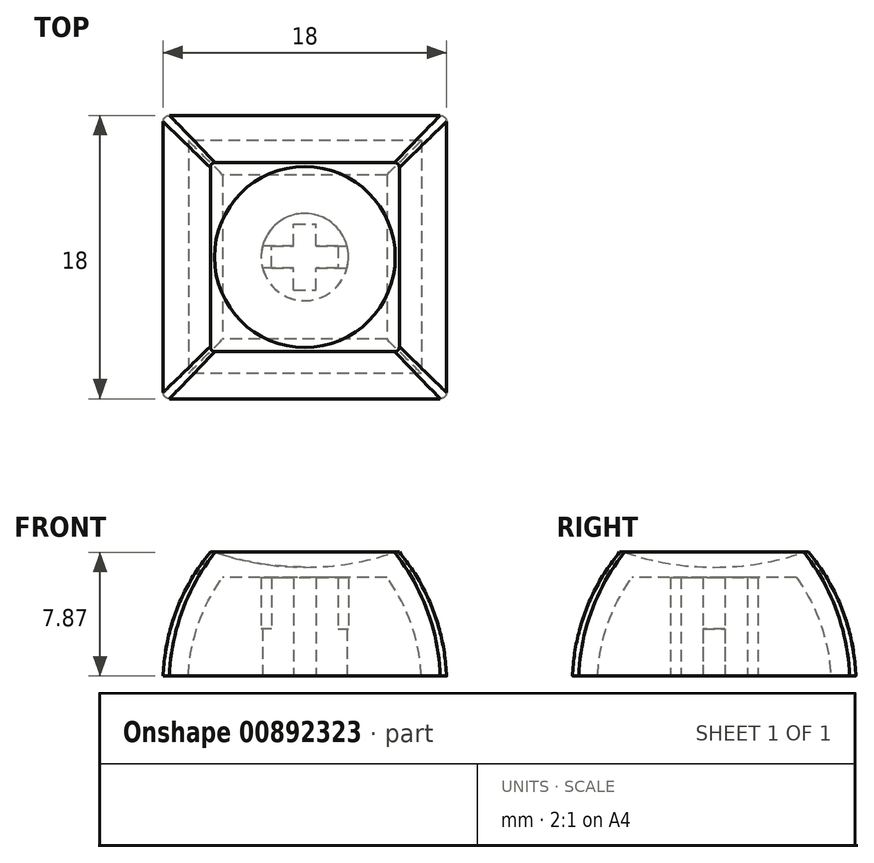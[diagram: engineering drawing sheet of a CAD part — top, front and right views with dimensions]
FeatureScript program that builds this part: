
annotation { "Feature Type Name" : "Feature", "Feature Type Description" : "" }
export const myFeature = defineFeature(function(context is Context, id is Id, definition is map)
    precondition{}
    {
        {
            var Q0;
            Q0=qCreatedBy(makeId("Top.planeOp"),FACE);
            var sketch = newSketch(context, id + "F0", { "sketchPlane" : qUnion([Q0])});
            skLineSegment(sketch, "E0.bottom", {"start": v(9, 9) * mm, "end": v(-9, 9) * mm});
            skLineSegment(sketch, "E0.top", {"start": v(9, -9) * mm, "end": v(-9, -9) * mm});
            skLineSegment(sketch, "E0.left", {"start": v(9, 9) * mm, "end": v(9, -9) * mm});
            skLineSegment(sketch, "E0.right", {"start": v(-9, 9) * mm, "end": v(-9, -9) * mm});
            skPoint(sketch, "E0.middle", {"position": v(0, 0) * mm});
            skSolve(sketch);
        }
        {
            var Q0;
            Q0=makeQuery(id+"F0.imprint","IMPRINT",FACE,{"disambiguationData":[TD([[makeQuery(id+"F0.imprint","IMPRINT",EDGE,{"derivedFrom":sQuery(id+"F0.wireOp",EDGE,"E0.bottom")}),1.0]])]});
            extrude(context, id + "F1", {"entities" : qUnion([Q0]), "depth" : 7.87 * mm, "offsetDistance" : 25 * mm});
        }
        {
            var Q0;
            Q0=makeQuery(id+"F1.opExtrude","SWEPT_FACE",FACE,{"disambiguationData":[OSD([sQuery(id+"F0.wireOp",EDGE,"E0.top")])]});
            var sketch = newSketch(context, id + "F2", { "sketchPlane" : qUnion([Q0])});
            skLineSegment(sketch, "E1", {"start": v(-9, 7.87) * mm, "end": v(-7.23, 6.1) * mm});
            skLineSegment(sketch, "E2", {"start": v(9, 7.87) * mm, "end": v(7.23, 6.1) * mm});
            skLineSegment(sketch, "E3", {"start": v(-9, 7.87) * mm, "end": v(-6, 7.87) * mm});
            skLineSegment(sketch, "E4", {"start": v(9, 7.87) * mm, "end": v(6, 7.87) * mm});
            skArc(sketch, "E5", {"start": v(-6, 7.87) * mm, "mid": v(-8.15, 4.18) * mm, "end": v(-9, 0) * mm});
            skArc(sketch, "E6", {"start": v(9, 0) * mm, "mid": v(8.15, 4.18) * mm, "end": v(6, 7.87) * mm});
            skLineSegment(sketch, "E7", {"start": v(-6, 7.87) * mm, "end": v(6, 7.87) * mm});
            skLineSegment(sketch, "E8", {"start": v(0, 7.87) * mm, "end": v(0, 7.17) * mm});
            skLineSegment(sketch, "E9", {"start": v(-6, 7.87) * mm, "end": v(-6, 7.87) * mm});
            skLineSegment(sketch, "E10", {"start": v(6, 7.87) * mm, "end": v(6, 7.87) * mm});
            skArc(sketch, "E11", {"start": v(-6, 7.87) * mm, "mid": v(0, 7.17) * mm, "end": v(6, 7.87) * mm});
            skSolve(sketch);
        }
        {
            var Q0;
            Q0=makeQuery(id+"F1.opExtrude","SWEPT_FACE",FACE,{"disambiguationData":[OSD([sQuery(id+"F0.wireOp",EDGE,"E0.right")])]});
            var sketch = newSketch(context, id + "F3", { "sketchPlane" : qUnion([Q0])});
            skLineSegment(sketch, "E12", {"start": v(-9, 7.87) * mm, "end": v(-7.23, 6.1) * mm});
            skLineSegment(sketch, "E13", {"start": v(9, 7.87) * mm, "end": v(7.23, 6.1) * mm});
            skLineSegment(sketch, "E14", {"start": v(-9, 7.87) * mm, "end": v(-6, 7.87) * mm});
            skLineSegment(sketch, "E15", {"start": v(9, 7.87) * mm, "end": v(6, 7.87) * mm});
            skArc(sketch, "E16", {"start": v(-6, 7.87) * mm, "mid": v(-8.15, 4.18) * mm, "end": v(-9, 0) * mm});
            skArc(sketch, "E17", {"start": v(9, 0) * mm, "mid": v(8.15, 4.18) * mm, "end": v(6, 7.87) * mm});
            skLineSegment(sketch, "E18", {"start": v(-6, 7.87) * mm, "end": v(-6, 7.87) * mm});
            skLineSegment(sketch, "E19", {"start": v(6, 7.87) * mm, "end": v(6, 7.87) * mm});
            skLineSegment(sketch, "E20", {"start": v(0, 7.87) * mm, "end": v(0, 7.17) * mm});
            skArc(sketch, "E21", {"start": v(-6, 7.87) * mm, "mid": v(0, 7.17) * mm, "end": v(6, 7.87) * mm});
            skSolve(sketch);
        }
        {
            var Q0;
            {var subQ0=sQuery(id+"F3.wireOp",EDGE,"E12");Q0=makeQuery(id+"F3.imprint","IMPRINT",FACE,{"disambiguationData":[TD([[makeQuery(id+"F3.imprint","IMPRINT",EDGE,{"derivedFrom":subQ0}),1.0]])]});}
            var Q1;
            {var subQ0=sQuery(id+"F3.wireOp",EDGE,"E12");Q1=makeQuery(id+"F3.imprint","IMPRINT",FACE,{"disambiguationData":[TD([[makeQuery(id+"F3.imprint","IMPRINT",EDGE,{"derivedFrom":subQ0}),-1.0]])]});}
            var Q2;
            {var subQ0=sQuery(id+"F3.wireOp",EDGE,"E13");Q2=makeQuery(id+"F3.imprint","IMPRINT",FACE,{"disambiguationData":[TD([[makeQuery(id+"F3.imprint","IMPRINT",EDGE,{"derivedFrom":subQ0}),-1.0]])]});}
            var Q3;
            {var subQ0=sQuery(id+"F3.wireOp",EDGE,"E13");Q3=makeQuery(id+"F3.imprint","IMPRINT",FACE,{"disambiguationData":[TD([[makeQuery(id+"F3.imprint","IMPRINT",EDGE,{"derivedFrom":subQ0}),1.0]])]});}
            extrude(context, id + "F4", {"entities" : qUnion([Q0, Q1, Q2, Q3]), "operationType" : NewBodyOperationType.REMOVE, "oppositeDirection" : true, "depth" : 25 * mm, "offsetDistance" : 25 * mm});
        }
        {
            var Q0;
            {var subQ0=sQuery(id+"F2.wireOp",EDGE,"E1");Q0=makeQuery(id+"F2.imprint","IMPRINT",FACE,{"disambiguationData":[TD([[makeQuery(id+"F2.imprint","IMPRINT",EDGE,{"derivedFrom":subQ0}),-1.0]])]});}
            var Q1;
            {var subQ0=sQuery(id+"F2.wireOp",EDGE,"E1");Q1=makeQuery(id+"F2.imprint","IMPRINT",FACE,{"disambiguationData":[TD([[makeQuery(id+"F2.imprint","IMPRINT",EDGE,{"derivedFrom":subQ0}),1.0]])]});}
            var Q2;
            {var subQ0=sQuery(id+"F2.wireOp",EDGE,"E2");Q2=makeQuery(id+"F2.imprint","IMPRINT",FACE,{"disambiguationData":[TD([[makeQuery(id+"F2.imprint","IMPRINT",EDGE,{"derivedFrom":subQ0}),-1.0]])]});}
            var Q3;
            {var subQ0=sQuery(id+"F2.wireOp",EDGE,"E2");Q3=makeQuery(id+"F2.imprint","IMPRINT",FACE,{"disambiguationData":[TD([[makeQuery(id+"F2.imprint","IMPRINT",EDGE,{"derivedFrom":subQ0}),1.0]])]});}
            extrude(context, id + "F5", {"entities" : qUnion([Q0, Q1, Q2, Q3]), "operationType" : NewBodyOperationType.REMOVE, "oppositeDirection" : true, "depth" : 25 * mm, "offsetDistance" : 25 * mm});
        }
        {
            var Q0;
            Q0=makeQuery(id+"F1.opExtrude","CAP_FACE",FACE,{"disambiguationData":[OSD([sQuery(id+"F0.wireOp",EDGE,"E0.bottom"),sQuery(id+"F0.wireOp",EDGE,"E0.top"),sQuery(id+"F0.wireOp",EDGE,"E0.left"),sQuery(id+"F0.wireOp",EDGE,"E0.right")])],"isStart":true});
            shell(context, id + "F6", {"entities" : qUnion([Q0]), "thickness" : 1.6 * mm});
        }
        {
            var Q0;
            Q0=makeQuery(id+"F1.opExtrude","CAP_FACE",FACE,{"disambiguationData":[OSD([sQuery(id+"F0.wireOp",EDGE,"E0.bottom"),sQuery(id+"F0.wireOp",EDGE,"E0.top"),sQuery(id+"F0.wireOp",EDGE,"E0.left"),sQuery(id+"F0.wireOp",EDGE,"E0.right")])],"isStart":true});
            var sketch = newSketch(context, id + "F7", { "sketchPlane" : qUnion([Q0])});
            skLineSegment(sketch, "E22.bottom", {"start": v(0, 0) * mm, "end": v(0.7, 0) * mm});
            skLineSegment(sketch, "E22.top", {"start": v(0, 2.1) * mm, "end": v(0.7, 2.1) * mm});
            skLineSegment(sketch, "E22.left", {"start": v(0, 0) * mm, "end": v(0, 2.1) * mm});
            skLineSegment(sketch, "E22.right", {"start": v(0.7, 0) * mm, "end": v(0.7, 2.1) * mm});
            skLineSegment(sketch, "E23.bottom", {"start": v(0, 0) * mm, "end": v(-0.7, 0) * mm});
            skLineSegment(sketch, "E23.top", {"start": v(0, 2.1) * mm, "end": v(-0.7, 2.1) * mm});
            skLineSegment(sketch, "E23.right", {"start": v(-0.7, 0) * mm, "end": v(-0.7, 2.1) * mm});
            skLineSegment(sketch, "E24.bottom", {"start": v(0, 0) * mm, "end": v(2.1, 0) * mm});
            skLineSegment(sketch, "E24.top", {"start": v(0, 0.7) * mm, "end": v(2.1, 0.7) * mm});
            skLineSegment(sketch, "E24.left", {"start": v(0, 0) * mm, "end": v(0, 0.7) * mm});
            skLineSegment(sketch, "E24.right", {"start": v(2.1, 0) * mm, "end": v(2.1, 0.7) * mm});
            skLineSegment(sketch, "E25.top", {"start": v(0, -0.7) * mm, "end": v(2.1, -0.7) * mm});
            skLineSegment(sketch, "E25.left", {"start": v(0, 0) * mm, "end": v(0, -0.7) * mm});
            skLineSegment(sketch, "E25.right", {"start": v(2.1, 0) * mm, "end": v(2.1, -0.7) * mm});
            skLineSegment(sketch, "E26.bottom", {"start": v(0, 0) * mm, "end": v(-2.1, 0) * mm});
            skLineSegment(sketch, "E26.top", {"start": v(0, 0.7) * mm, "end": v(-2.1, 0.7) * mm});
            skLineSegment(sketch, "E26.right", {"start": v(-2.1, 0) * mm, "end": v(-2.1, 0.7) * mm});
            skLineSegment(sketch, "E27.top", {"start": v(0, -0.7) * mm, "end": v(-2.1, -0.7) * mm});
            skLineSegment(sketch, "E27.right", {"start": v(-2.1, 0) * mm, "end": v(-2.1, -0.7) * mm});
            skLineSegment(sketch, "E28.bottom", {"start": v(-0.7, 0) * mm, "end": v(0, 0) * mm});
            skLineSegment(sketch, "E28.top", {"start": v(-0.7, -2.1) * mm, "end": v(0, -2.1) * mm});
            skLineSegment(sketch, "E28.left", {"start": v(-0.7, 0) * mm, "end": v(-0.7, -2.1) * mm});
            skLineSegment(sketch, "E28.right", {"start": v(0, 0) * mm, "end": v(0, -2.1) * mm});
            skLineSegment(sketch, "E29.bottom", {"start": v(0.7, 0) * mm, "end": v(0, 0) * mm});
            skLineSegment(sketch, "E29.top", {"start": v(0.7, -2.1) * mm, "end": v(0, -2.1) * mm});
            skLineSegment(sketch, "E29.left", {"start": v(0.7, 0) * mm, "end": v(0.7, -2.1) * mm});
            skCircle(sketch, "E30", {"center": v(0, 0) * mm, "radius": 2.77 * mm});
            skSolve(sketch);
        }
        {
            var Q0;
            {var subQ12=sQuery(id+"F7.wireOp",EDGE,"E22.top");Q0=makeQuery(id+"F7.imprint","IMPRINT",FACE,{"disambiguationData":[TD([[makeQuery(id+"F7.imprint","IMPRINT",EDGE,{"derivedFrom":subQ12}),1.0]])]});}
            extrude(context, id + "F8", {"entities" : qUnion([Q0]), "operationType" : NewBodyOperationType.ADD, "oppositeDirection" : true, "depth" : 7 * mm, "offsetDistance" : 25 * mm});
        }
        {
            var Q0;
            Q0=makeQuery(id+"F8.opExtrude","CAP_FACE",FACE,{"disambiguationData":[OSD([sQuery(id+"F7.wireOp",EDGE,"E22.top"),sQuery(id+"F7.wireOp",EDGE,"E22.right"),sQuery(id+"F7.wireOp",EDGE,"E23.top"),sQuery(id+"F7.wireOp",EDGE,"E23.right"),sQuery(id+"F7.wireOp",EDGE,"E24.top"),sQuery(id+"F7.wireOp",EDGE,"E24.right"),sQuery(id+"F7.wireOp",EDGE,"E25.top"),sQuery(id+"F7.wireOp",EDGE,"E25.right"),sQuery(id+"F7.wireOp",EDGE,"E26.top"),sQuery(id+"F7.wireOp",EDGE,"E26.right"),sQuery(id+"F7.wireOp",EDGE,"E27.top"),sQuery(id+"F7.wireOp",EDGE,"E27.right"),sQuery(id+"F7.wireOp",EDGE,"E28.top"),sQuery(id+"F7.wireOp",EDGE,"E28.left"),sQuery(id+"F7.wireOp",EDGE,"E29.top"),sQuery(id+"F7.wireOp",EDGE,"E29.left"),sQuery(id+"F7.wireOp",EDGE,"E30")])],"isStart":true});
            var sketch = newSketch(context, id + "F9", { "sketchPlane" : qUnion([Q0])});
            skLineSegment(sketch, "E31", {"start": v(-2.1, 0.7) * mm, "end": v(-2.68, 0.7) * mm});
            skLineSegment(sketch, "E32", {"start": v(-2.1, -0.7) * mm, "end": v(-2.68, -0.7) * mm});
            skLineSegment(sketch, "E33", {"start": v(2.1, -0.7) * mm, "end": v(2.68, -0.7) * mm});
            skLineSegment(sketch, "E34", {"start": v(2.1, 0.7) * mm, "end": v(2.68, 0.7) * mm});
            skCircle(sketch, "E35", {"center": v(0, 0) * mm, "radius": 2.77 * mm});
            skSolve(sketch);
        }
        {
            var Q0;
            {var subQ0=sQuery(id+"F9.wireOp",EDGE,"E31");Q0=makeQuery(id+"F9.imprint","IMPRINT",FACE,{"disambiguationData":[TD([[makeQuery(id+"F9.imprint","IMPRINT",EDGE,{"derivedFrom":subQ0}),1.0]])]});}
            var Q1;
            {var subQ0=sQuery(id+"F9.wireOp",EDGE,"E33");Q1=makeQuery(id+"F9.imprint","IMPRINT",FACE,{"disambiguationData":[TD([[makeQuery(id+"F9.imprint","IMPRINT",EDGE,{"derivedFrom":subQ0}),1.0]])]});}
            extrude(context, id + "F10", {"entities" : qUnion([Q0, Q1]), "operationType" : NewBodyOperationType.REMOVE, "oppositeDirection" : true, "depth" : 3 * mm, "offsetDistance" : 25 * mm});
        }
        {
            var Q0;
            Q0=makeQuery(id+"F5.boolean.opBoolean","COPY",EDGE,{"derivedFrom":makeQuery(id+"F5.opExtrude","SWEPT_EDGE",EDGE,{"disambiguationData":[OSD([sQuery(id+"F2.wireOp",EDGE,"E4"),sQuery(id+"F2.wireOp",EDGE,"E6"),sQuery(id+"F2.wireOp",EDGE,"E7"),sQuery(id+"F2.wireOp",EDGE,"E11")])]})});
            var Q1;
            Q1=makeQuery(id+"F4.boolean.opBoolean","COPY",EDGE,{"derivedFrom":makeQuery(id+"F4.opExtrude","SWEPT_EDGE",EDGE,{"disambiguationData":[OSD([sQuery(id+"F0.wireOp",EDGE,"E0.right"),sQuery(id+"F3.wireOp",EDGE,"E15"),sQuery(id+"F3.wireOp",EDGE,"E17"),sQuery(id+"F3.wireOp",EDGE,"E21")])]})});
            var Q2;
            Q2=makeQuery(id+"F4.boolean.opBoolean","COPY",EDGE,{"derivedFrom":makeQuery(id+"F4.opExtrude","SWEPT_EDGE",EDGE,{"disambiguationData":[OSD([sQuery(id+"F0.wireOp",EDGE,"E0.right"),sQuery(id+"F3.wireOp",EDGE,"E14"),sQuery(id+"F3.wireOp",EDGE,"E16"),sQuery(id+"F3.wireOp",EDGE,"E21")])]})});
            var Q3;
            Q3=makeQuery(id+"F5.boolean.opBoolean","COPY",EDGE,{"derivedFrom":makeQuery(id+"F5.opExtrude","SWEPT_EDGE",EDGE,{"disambiguationData":[OSD([sQuery(id+"F2.wireOp",EDGE,"E3"),sQuery(id+"F2.wireOp",EDGE,"E5"),sQuery(id+"F2.wireOp",EDGE,"E7"),sQuery(id+"F2.wireOp",EDGE,"E11")])]})});
            var Q4;
            Q4=makeQuery(id+"F5.boolean.opBoolean","INTERSECT",EDGE,{"derivedFrom":[makeQuery(id+"F4.boolean.opBoolean","COPY",FACE,{"derivedFrom":makeQuery(id+"F4.opExtrude","SWEPT_FACE",FACE,{"disambiguationData":[OSD([sQuery(id+"F3.wireOp",EDGE,"E16")])]})}),makeQuery(id+"F5.opExtrude","SWEPT_FACE",FACE,{"disambiguationData":[OSD([sQuery(id+"F2.wireOp",EDGE,"E6")])]})]});
            var Q5;
            Q5=makeQuery(id+"F5.boolean.opBoolean","INTERSECT",EDGE,{"derivedFrom":[makeQuery(id+"F4.boolean.opBoolean","COPY",FACE,{"derivedFrom":makeQuery(id+"F4.opExtrude","SWEPT_FACE",FACE,{"disambiguationData":[OSD([sQuery(id+"F3.wireOp",EDGE,"E17")])]})}),makeQuery(id+"F5.opExtrude","SWEPT_FACE",FACE,{"disambiguationData":[OSD([sQuery(id+"F2.wireOp",EDGE,"E6")])]})]});
            var Q6;
            Q6=makeQuery(id+"F5.boolean.opBoolean","INTERSECT",EDGE,{"derivedFrom":[makeQuery(id+"F4.boolean.opBoolean","COPY",FACE,{"derivedFrom":makeQuery(id+"F4.opExtrude","SWEPT_FACE",FACE,{"disambiguationData":[OSD([sQuery(id+"F3.wireOp",EDGE,"E17")])]})}),makeQuery(id+"F5.opExtrude","SWEPT_FACE",FACE,{"disambiguationData":[OSD([sQuery(id+"F2.wireOp",EDGE,"E5")])]})]});
            var Q7;
            Q7=makeQuery(id+"F5.boolean.opBoolean","INTERSECT",EDGE,{"derivedFrom":[makeQuery(id+"F4.boolean.opBoolean","COPY",FACE,{"derivedFrom":makeQuery(id+"F4.opExtrude","SWEPT_FACE",FACE,{"disambiguationData":[OSD([sQuery(id+"F3.wireOp",EDGE,"E16")])]})}),makeQuery(id+"F5.opExtrude","SWEPT_FACE",FACE,{"disambiguationData":[OSD([sQuery(id+"F2.wireOp",EDGE,"E5")])]})]});
            fillet(context, id + "F11", {"entities" : qUnion([Q0, Q1, Q2, Q3, Q4, Q5, Q6, Q7]), "radius" : .4 * mm, "tangentPropagation" : true, "allowEdgeOverflow" : false});
        }
        {
            var Q0;
            Q0=qCreatedBy(makeId("Front.planeOp"),FACE);
            var sketch = newSketch(context, id + "F12", { "sketchPlane" : qUnion([Q0])});
            skLineSegment(sketch, "E36", {"start": v(0, 0) * mm, "end": v(0, 10) * mm});
            skLineSegment(sketch, "E37", {"start": v(0, 10) * mm, "end": v(10, 10) * mm});
            skLineSegment(sketch, "E38", {"start": v(0, 10) * mm, "end": v(-10, 10) * mm});
            skArc(sketch, "E39", {"start": v(-10, 10) * mm, "mid": v(0, 6.92) * mm, "end": v(10, 10) * mm});
            skSolve(sketch);
        }
        {
            var Q0;
            {var subQ0=sQuery(id+"F12.wireOp",EDGE,"E38");Q0=makeQuery(id+"F12.imprint","IMPRINT",FACE,{"disambiguationData":[TD([[makeQuery(id+"F12.imprint","IMPRINT",EDGE,{"derivedFrom":subQ0}),1.0]])]});}
            var Q1;
            Q1=sQuery(id+"F12.wireOp",EDGE,"E36");
            revolve(context, id + "F13", {"operationType" : NewBodyOperationType.REMOVE, "surfaceOperationType" : NewSurfaceOperationType.NEW, "entities" : qUnion([Q0]), "axis" : qUnion([Q1]), "revolveType" : RevolveType.FULL, "oppositeDirection" : true});
        }
    });
